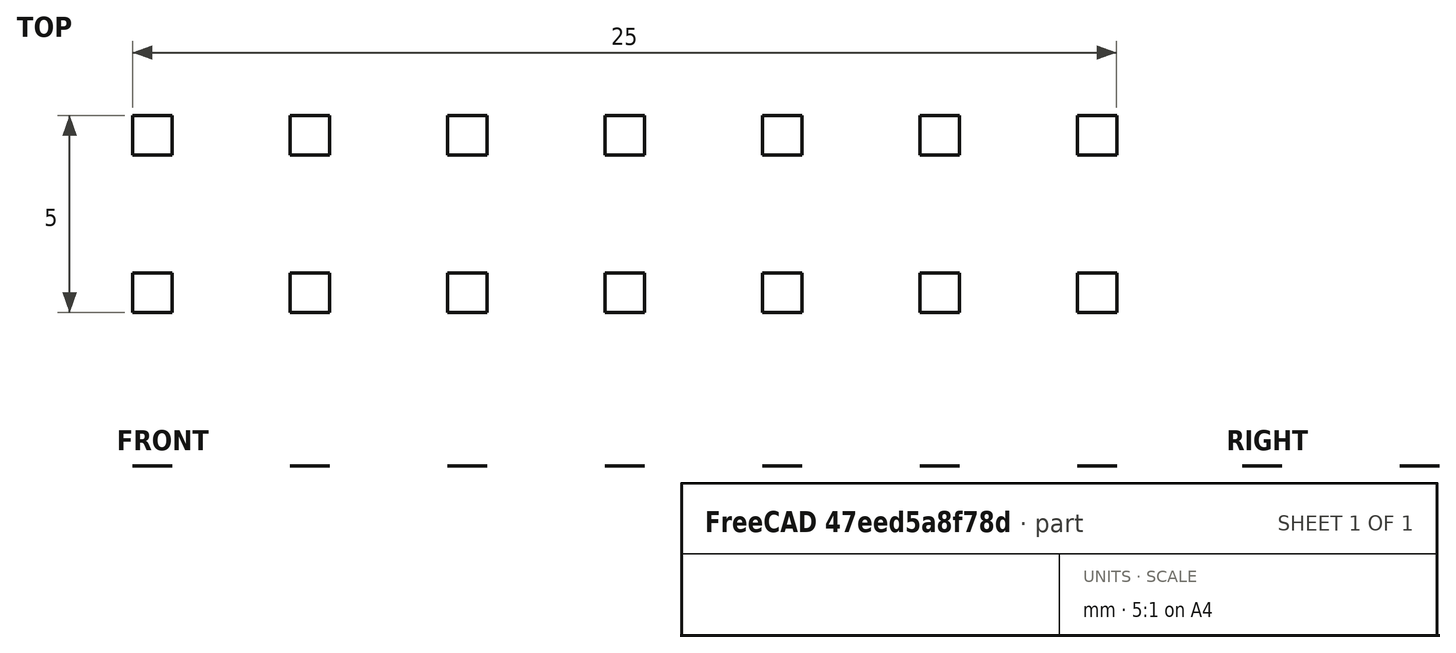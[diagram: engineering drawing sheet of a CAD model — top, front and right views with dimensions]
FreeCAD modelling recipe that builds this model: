
FCSTD DOCUMENT  (FreeCAD 0.16R6706 (Git))
Label: IoT_Front_Label
License: All rights reserved
LicenseURL: http://en.wikipedia.org/wiki/All_rights_reserved
objects: App::Annotation×39, Part::Part2DObjectPython×10, Drawing::FeatureViewPython×8, App::DocumentObjectGroup×6, Part::FeaturePython×1, Drawing::FeatureViewSymbol×1, Drawing::FeaturePage×1
note: 11 computed .brp shape members not serialized (recipe doc carries the construction recipe); baked Part::Feature solids carry a one-line shape summary decoded from their .brp

FEATURE [Part::Part2DObjectPython] Rectangle  label="Obrys"  # Draft 2D object (typed FeaturePython)
  ChamferSize = 0
  FilletRadius = 0
  Height = 155.7
  Length = 64.88
  MakeFace = false
FEATURE [Part::Part2DObjectPython] Circle  label="StatusLed"  # Draft 2D object (typed FeaturePython)
  FirstAngle = 0
  LastAngle = 0
  MakeFace = false
  Placement = pos=(58.7,104.6,0) rot=(0,0,1;0rad)
  Radius = 3
FEATURE [Part::Part2DObjectPython] Circle001  label="PwrLed"  # Draft 2D object (typed FeaturePython)
  FirstAngle = 0
  LastAngle = 0
  MakeFace = false
  Placement = pos=(58.7,97,0) rot=(0,0,1;0rad)
  Radius = 3
FEATURE [Part::Part2DObjectPython] Circle002  label="Reset"  # Draft 2D object (typed FeaturePython)
  FirstAngle = 0
  LastAngle = 0
  MakeFace = false
  Placement = pos=(32,108.4,0) rot=(0,0,1;0rad)
  Radius = 1.5
FEATURE [Part::Part2DObjectPython] Rectangle001  label="Vypinac"  # Draft 2D object (typed FeaturePython)
  ChamferSize = 0
  FilletRadius = 0
  Height = 14
  Length = 8
  MakeFace = false
  Placement = pos=(54,62.5,0) rot=(0,0,1;0rad)
FEATURE [App::DocumentObjectGroup] Group  label="MainGeometry"
  Group = -> [Rectangle,Circle,Circle001,Circle002,Rectangle001]
FEATURE [App::Annotation] Text  label="ResetLabel"
  LabelText = RESET
  Position = (28.5,104,0)
FEATURE [App::Annotation] Text001  label="StatusLabel"
  LabelText = STATUS
  Position = (46.52,104,0)
FEATURE [App::Annotation] Text002  label="PwrLabel"
  LabelText = POWER
  Position = (47,96,0)
FEATURE [App::DocumentObjectGroup] Group001  label="LedLabels"
  Group = -> [Text001,Text002]
FEATURE [App::Annotation] Text003  label="Title"
  LabelText = IoT Module
  Position = (19,143,0)
FEATURE [Part::Part2DObjectPython] Rectangle002  label="Pin"  # Draft 2D object (typed FeaturePython)
  ChamferSize = 0
  Columns = 1
  FilletRadius = 0
  Height = -1
  Length = 1
  MakeFace = true
  Placement = pos=(19.9424,10,0) rot=(0,0,1;0rad)
  Rows = 1
FEATURE [Part::FeaturePython] Array  label="Pins"  # Draft array (typed FeaturePython)
  Angle = 360
  ArrayType = 0
  Axis = (0,0,0)
  Base = -> Rectangle002
  Center = (0,0,0)
  Fuse = false
  IntervalAxis = (0,0,0)
  IntervalX = (4,0,0)
  IntervalY = (0,4,0)
  IntervalZ = (0,0,0)
  NumberPolar = 0
  NumberX = 7
  NumberY = 2
  NumberZ = 0
  Placement = pos=(-0.0575695,4,0) rot=(0,0,1;0rad)
FEATURE [Part::Part2DObjectPython] Rectangle003  label="Closure"  # Draft 2D object (typed FeaturePython)
  ChamferSize = 0
  Columns = 1
  FilletRadius = 0
  Height = -9
  Length = 29
  MakeFace = true
  Placement = pos=(17.9424,20,0) rot=(0,0,1;0rad)
  Rows = 1
FEATURE [Part::Part2DObjectPython] Rectangle004  label="Locker"  # Draft 2D object (typed FeaturePython)
  ChamferSize = 0
  Columns = 1
  FilletRadius = 0
  Height = -1
  Length = 4.95284
  MakeFace = true
  Placement = pos=(29.9896,20,0) rot=(0,0,1;0rad)
  Rows = 1
FEATURE [App::DocumentObjectGroup] Group002  label="ConnectorGeometry"
  Group = -> [Array,Rectangle002,Rectangle003,Rectangle004]
FEATURE [App::Annotation] Text004  label="Pin13"
  LabelText = VIN
  Position = (20.94,21,1)
FEATURE [App::Annotation] Text005  label="Pin11"
  LabelText = RST
  Position = (24.9424,21,0)
FEATURE [App::Annotation] Text006  label="Pin9"
  LabelText = GPIO14
  Position = (28.9424,21,0)
FEATURE [App::Annotation] Text007  label="Pin7"
  LabelText = GPIO12
  Position = (32.9424,21,0)
FEATURE [App::Annotation] Text008  label="Pin5"
  LabelText = GPIO4
  Position = (36.9424,21,0)
FEATURE [App::Annotation] Text009  label="Pin3"
  LabelText = GPIO1/TX
  Position = (40.9424,21,0)
FEATURE [App::Annotation] Text010  label="Pin1"
  LabelText = +5V
  Position = (44.9424,21,0)
FEATURE [App::Annotation] Text011  label="Pin14"
  LabelText = GND
  Position = (20.9424,10,0)
FEATURE [App::Annotation] Text012  label="Pin12"
  LabelText = ADC
  Position = (24.9424,10,0)
FEATURE [App::Annotation] Text013  label="Pin10"
  LabelText = GPIO16
  Position = (28.9424,10,0)
FEATURE [App::Annotation] Text014  label="Pin8"
  LabelText = GPIO13
  Position = (32.9424,10,0)
FEATURE [App::Annotation] Text015  label="Pin6"
  LabelText = GPIO5
  Position = (36.9424,10,0)
FEATURE [App::Annotation] Text016  label="Pin4"
  LabelText = GPIO3/RX
  Position = (40.9424,10,0)
FEATURE [App::Annotation] Text017  label="Pin2"
  LabelText = +3.3V
  Position = (44.9424,10,0)
FEATURE [App::Annotation] Text018  label="PinHelper1"
  LabelText = 1
  Position = (46,18,0)
FEATURE [App::Annotation] Text019  label="PinHelper2"
  LabelText = 2
  Position = (46,12,0)
FEATURE [App::Annotation] Text020  label="PinHelper14"
  LabelText = 14
  Position = (18.5,12,0)
FEATURE [App::DocumentObjectGroup] Group003  label="ConnectorLabels"
  Group = -> [Text004,Text005,Text006,Text007,Text008,Text009,Text010,Text011,Text012,Text013,Text014,Text015,Text016,Text017]
FEATURE [App::DocumentObjectGroup] Group004  label="ConnectorTextHelpers"
  Group = -> [Text018,Text019,Text020]
FEATURE [Drawing::FeatureViewPython] ViewGroup001  label="ViewLedLabels"  # drawing view (typed FeaturePython)
  Direction = (0,0,0)
  FillStyle = 0
  FontSize = 4
  LineStyle = 0
  LineWidth = 0.35
  Rotation = 0
  Source = -> Group001
  ViewResult = <g id="ViewGroup001" transform="rotate(0.0,69.0,200.0) translate(69.0,200.0) scale(1.0,-1.0)"><text fill="#000000" font-size="2.0" style="text-anchor:start;text-align:left;font-family:Arial" transform="rotate(0.0,46.52,104.0) translate(46.52,104.0) scale(1,-1) " freecad:skip="1">\nSTATUS</text>\n<text fill="#000000" font-size="2.0" style="text-anchor:start;text-align:left;font-family:Arial" transform="rotate(0.0,47.0,96.0) translate(47.0,96.0) scale(1,-1) " freecad:skip="1">\nPOWER</text>\n</g>
  Visible = true
  X = 69
  Y = 200
FEATURE [Drawing::FeatureViewPython] ViewGroup002  label="ViewConnGeometry"  # drawing view (typed FeaturePython)
  Direction = (0,0,0)
  FillStyle = 0
  FontSize = 12
  LineStyle = 0
  LineWidth = 0.35
  Rotation = 0
  Source = -> Group002
  ViewResult = <blob: 4496 chars omitted>
  Visible = true
  X = 70
  Y = 200
FEATURE [Drawing::FeatureViewPython] ViewGroup003  label="ViewConnLabels"  # drawing view (typed FeaturePython)
  Direction = (0,0,0)
  FillStyle = 0
  FontSize = 3.6
  LineStyle = 0
  LineWidth = 0.35
  Rotation = 0
  Source = -> Group003
  ViewResult = <blob: 3085 chars omitted>
  Visible = true
  X = 70
  Y = 200
FEATURE [Drawing::FeatureViewPython] ViewGroup004  label="ViewConnTextHelpers"  # drawing view (typed FeaturePython)
  Direction = (0,0,0)
  FillStyle = 0
  FontSize = 2
  LineStyle = 0
  LineWidth = 0.35
  Rotation = 0
  Source = -> Group004
  ViewResult = <g id="ViewGroup004" transform="rotate(0.0,70.0,200.0) translate(70.0,200.0) scale(1.0,-1.0)"><text fill="#000000" font-size="1.0" style="text-anchor:start;text-align:left;font-family:Arial" transform="rotate(0.0,46.0,18.0) translate(46.0,18.0) scale(1,-1) " freecad:skip="1">\n1</text>\n<text fill="#000000" font-size="1.0" style="text-anchor:start;text-align:left;font-family:Arial" transform="rotate(0.0,46.0,12.0) translate(46.0,12.0) scale(1,-1) " freecad:skip="1">\n2</text>\n<text fill="#000000" font-size="1.0" style="text-anchor:start;text-align:left;font-family:Arial" transform="rotate(0.0,18.5,12.0) translate(18.5,12.0) scale(1,-1) " freecad:skip="1">\n14</text>\n</g>
  Visible = true
  X = 70
  Y = 200
FEATURE [Drawing::FeatureViewPython] ViewText003  label="ViewTitle"  # drawing view (typed FeaturePython)
  Direction = (0,0,0)
  FillStyle = 0
  FontSize = 12
  LineStyle = 0
  LineWidth = 0.35
  Rotation = 0
  Source = -> Text003
  ViewResult = <g id="ViewText003" transform="rotate(0.0,70.0,200.0) translate(70.0,200.0) scale(1.0,-1.0)"><text fill="#000000" font-size="6.0" style="text-anchor:start;text-align:left;font-family:Arial" transform="rotate(0.0,19.0,143.0) translate(19.0,143.0) scale(1,-1) " freecad:skip="1">\nIoT Module</text>\n</g>
  Visible = true
  X = 70
  Y = 200
FEATURE [Drawing::FeatureViewPython] ViewText  label="ViewReset"  # drawing view (typed FeaturePython)
  Direction = (0,0,0)
  FillStyle = 0
  FontSize = 4
  LineStyle = 0
  LineWidth = 0.35
  Rotation = 0
  Source = -> Text
  ViewResult = <g id="ViewText" transform="rotate(0.0,70.25,200.0) translate(70.25,200.0) scale(1.0,-1.0)"><text fill="#000000" font-size="2.0" style="text-anchor:start;text-align:left;font-family:Arial" transform="rotate(0.0,28.5,104.0) translate(28.5,104.0) scale(1,-1) " freecad:skip="1">\nRESET</text>\n</g>
  Visible = true
  X = 70.25
  Y = 200
FEATURE [Drawing::FeatureViewPython] ViewGroup  label="ViewGeometry"  # drawing view (typed FeaturePython)
  Direction = (0,0,0)
  FillStyle = 0
  FontSize = 12
  LineStyle = 0
  LineWidth = 1.7
  Rotation = 0
  Source = -> Group
  ViewResult = <g id="ViewGroup" transform="rotate(0.0,70.0,200.0) translate(70.0,200.0) scale(1.0,-1.0)"><path id="Rectangle_w0000"  d="M 0.0 0.0 L 64.88 0.0 L 64.88 155.7 L 0.0 155.7 L 0.0 0.0 " stroke="#000000" stroke-width="1.7 px" style="stroke-width:1.7;stroke-miterlimit:4;stroke-dasharray:none;fill:none;fill-rule: evenodd "/>\n<circle cx="58.7000007629" cy="104.599998474" r="3.0" stroke="#000000" stroke-width="1.7 px" style="stroke-width:1.7;stroke-miterlimit:4;stroke-dasharray:none;fill:none"/>\n<circle cx="58.7000007629" cy="97.0" r="3.0" stroke="#000000" stroke-width="1.7 px" style="stroke-width:1.7;stroke-miterlimit:4;stroke-dasharray:none;fill:none"/>\n<circle cx="32.0" cy="108.400001526" r="1.5" stroke="#000000" stroke-width="1.7 px" style="stroke-width:1.7;stroke-miterlimit:4;stroke-dasharray:none;fill:none"/>\n<path id="Rectangle001_w0000"  d="M 54.0 62.5 L 62.0 62.5 L 62.0 76.5 L 54.0 76.5 L 54.0 62.5 " stroke="#000000" stroke-width="1.7 px" style="stroke-width:1.7;stroke-miterlimit:4;stroke-dasharray:none;fill:none;fill-rule: evenodd "/>\n</g>
  Visible = true
  X = 70
  Y = 200
FEATURE [Drawing::FeatureViewSymbol] Symbol  label="WifiSymbol"
  Rotation = 0
  Scale = 0.05
  Symbol = <blob: 8522 chars omitted>
  ViewResult = <blob: 8583 chars omitted>
  Visible = true
  X = 95
  Y = 62
FEATURE [App::Annotation] Text021  label="Index"
  LabelText = Index
  Position = (6.9576,59.4976,0)
FEATURE [App::Annotation] Text022  label="GpioText"
  LabelText = GPIO
  Position = (15.9576,59.4976,0)
FEATURE [Part::Part2DObjectPython] Line  label="LineTableVert"  # Draft 2D object (typed FeaturePython)
  ChamferSize = 0
  Closed = false
  End = (13.9576,33.4976,0)
  FilletRadius = 0
  Length = 27
  MakeFace = true
  Placement = pos=(-3.0424,-30.5024,0) rot=(0,0,1;0rad)
  Points = (2) [(17,91,0),(17,64,0)]
  Start = (13.9576,60.4976,0)
  Subdivisions = 0
FEATURE [Part::Part2DObjectPython] Line001  label="LineTableHor"  # Draft 2D object (typed FeaturePython)
  ChamferSize = 0
  Closed = false
  End = (24.9576,58.4976,0)
  FilletRadius = 0
  Length = 19
  MakeFace = true
  Placement = pos=(-3.0424,-30.5024,0) rot=(0,0,1;0rad)
  Points = (2) [(9,89,0),(28,89,0)]
  Start = (5.9576,58.4976,0)
  Subdivisions = 0
FEATURE [App::Annotation] Text023  label="GPIO1"
  LabelText = GPIO1
  Position = (15.9576,55.4976,0)
FEATURE [App::Annotation] Text024  label="GPIO3"
  LabelText = GPIO3
  Position = (15.9576,52.4976,0)
FEATURE [App::Annotation] Text025  label="GPIO4"
  LabelText = GPIO4
  Position = (15.9576,49.4976,0)
FEATURE [App::Annotation] Text026  label="GPIO5"
  LabelText = GPIO5
  Position = (15.9576,46.4976,0)
FEATURE [App::Annotation] Text027  label="GPIO12"
  LabelText = GPIO12
  Position = (15.9576,43.4976,0)
FEATURE [App::Annotation] Text028  label="GPIO13"
  LabelText = GPIO13
  Position = (15.9576,40.4976,0)
FEATURE [App::Annotation] Text029  label="GPIO14"
  LabelText = GPIO14
  Position = (15.9576,37.4976,0)
FEATURE [App::Annotation] Text030  label="GPIO16"
  LabelText = GPIO16
  Position = (15.9576,34.4976,0)
FEATURE [App::Annotation] Text031  label="Index0"
  LabelText = 0
  Position = (11.9576,34.4976,0)
FEATURE [App::Annotation] Text032  label="Index10"
  LabelText = 10
  Position = (11.9576,55.4976,0)
FEATURE [App::Annotation] Text033  label="Index9"
  LabelText = 9
  Position = (11.9576,52.4976,0)
FEATURE [App::Annotation] Text034  label="Index2"
  LabelText = 2
  Position = (11.9576,49.4976,0)
FEATURE [App::Annotation] Text035  label="Index1"
  LabelText = 1
  Position = (10.9576,46.4976,0)
FEATURE [App::Annotation] Text036  label="Index6"
  LabelText = 6
  Position = (10.9576,43.4976,0)
FEATURE [App::Annotation] Text037  label="Index7"
  LabelText = 7
  Position = (10.9576,40.4976,0)
FEATURE [App::Annotation] Text038  label="Index5"
  LabelText = 5
  Position = (10.9576,37.4976,0)
FEATURE [App::DocumentObjectGroup] Group005  label="GpioTable"
  Group = -> [Text021,Line,Line001,Text022,Text023,Text024,Text025,Text026,Text027,Text028,Text029,Text030,Text031,Text032,Text033,Text034,Text035,Text036,Text037,Text038]
FEATURE [Drawing::FeatureViewPython] ViewGroup005  label="ViewGpioTable"  # drawing view (typed FeaturePython)
  Direction = (0,0,0)
  FillStyle = 0
  FontSize = 4
  LineStyle = 0
  LineWidth = 0.35
  Rotation = 0
  Source = -> Group005
  ViewResult = <blob: 4701 chars omitted>
  Visible = true
  X = 70
  Y = 200
FEATURE [Drawing::FeaturePage] Page  label="Drawing"
  Group = -> [ViewGroup001,ViewGroup002,ViewGroup003,ViewGroup004,ViewText003,ViewText,ViewGroup,Symbol,ViewGroup005]
